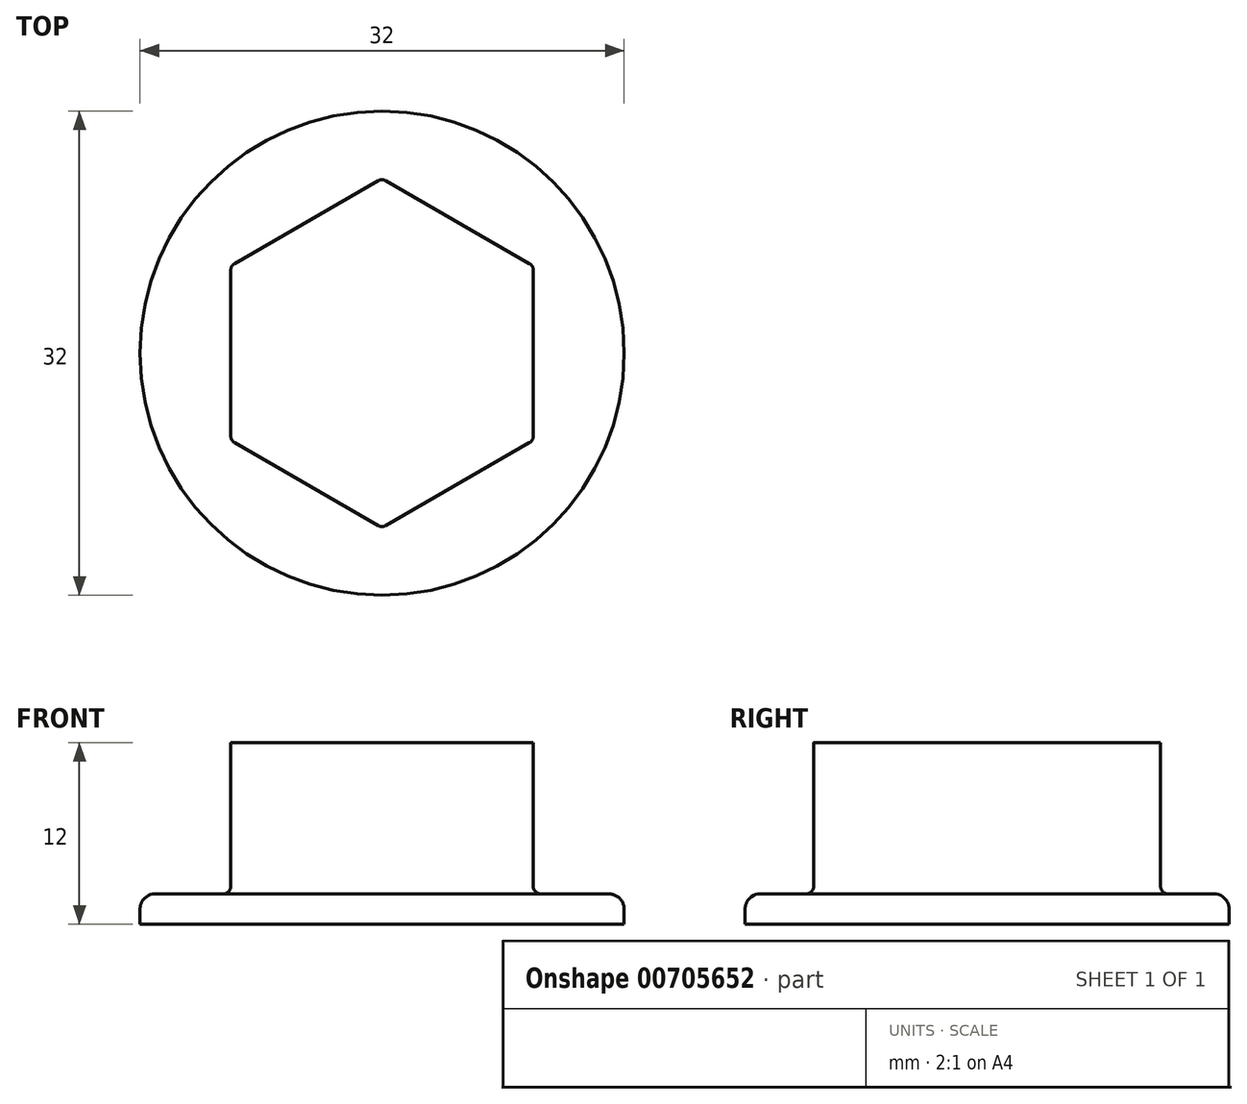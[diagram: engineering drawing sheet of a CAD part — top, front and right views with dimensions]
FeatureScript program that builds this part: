
annotation { "Feature Type Name" : "Feature", "Feature Type Description" : "" }
export const myFeature = defineFeature(function(context is Context, id is Id, definition is map)
    precondition{}
    {
        {
            var Q0;
            Q0=qCreatedBy(makeId("Top.planeOp"),FACE);
            var sketch = newSketch(context, id + "F0", { "sketchPlane" : qUnion([Q0])});
            skCircle(sketch, "E0", {"center": v(0, 0) * mm, "radius": 16 * mm});
            skCircle(sketch, "E1.cCircle", {"center": v(0, 0) * mm, "radius": 10 * mm, "construction": true});
            skLineSegment(sketch, "E1.0", {"start": v(10, -5.77) * mm, "end": v(0, -11.55) * mm});
            skLineSegment(sketch, "E1.1", {"start": v(0, -11.55) * mm, "end": v(-10, -5.77) * mm});
            skLineSegment(sketch, "E1.2", {"start": v(-10, -5.77) * mm, "end": v(-10, 5.77) * mm});
            skLineSegment(sketch, "E1.3", {"start": v(-10, 5.77) * mm, "end": v(0, 11.55) * mm});
            skLineSegment(sketch, "E1.4", {"start": v(0, 11.55) * mm, "end": v(10, 5.77) * mm});
            skLineSegment(sketch, "E1.5", {"start": v(10, 5.77) * mm, "end": v(10, -5.77) * mm});
            skPoint(sketch, "E1.0.midPoint", {"position": v(5, -8.66) * mm});
            skSolve(sketch);
        }
        {
            var Q0;
            Q0=makeQuery(id+"F0.imprint","IMPRINT",FACE,{"disambiguationData":[TD([[makeQuery(id+"F0.imprint","IMPRINT",EDGE,{"derivedFrom":sQuery(id+"F0.wireOp",EDGE,"E0")}),1.0]])]});
            var Q1;
            Q1=makeQuery(id+"F0.imprint","IMPRINT",FACE,{"disambiguationData":[TD([[makeQuery(id+"F0.imprint","IMPRINT",EDGE,{"derivedFrom":sQuery(id+"F0.wireOp",EDGE,"E1.0")}),-1.0]])]});
            extrude(context, id + "F1", {"entities" : qUnion([Q0, Q1]), "depth" : 2 * mm, "offsetDistance" : 25 * mm});
        }
        {
            var Q0;
            Q0=makeQuery(id+"F1.opExtrude","CAP_EDGE",EDGE,{"disambiguationData":[OSD([sQuery(id+"F0.wireOp",EDGE,"E0")])],"isStart":false});
            fillet(context, id + "F2", {"entities" : qUnion([Q0]), "radius" : 1 * mm, "tangentPropagation" : true, "allowEdgeOverflow" : false});
        }
        {
            var Q0;
            Q0=makeQuery(id+"F0.imprint","IMPRINT",FACE,{"disambiguationData":[TD([[makeQuery(id+"F0.imprint","IMPRINT",EDGE,{"derivedFrom":sQuery(id+"F0.wireOp",EDGE,"E1.0")}),-1.0]])]});
            extrude(context, id + "F3", {"entities" : qUnion([Q0]), "operationType" : NewBodyOperationType.ADD, "depth" : 12 * mm, "offsetDistance" : 25 * mm});
        }
        {
            var Q0;
            Q0=makeQuery(id+"F3.boolean.opBoolean","INTERSECT",EDGE,{"derivedFrom":[makeQuery(id+"F1.opExtrude","CAP_FACE",FACE,{"disambiguationData":[OSD([sQuery(id+"F0.wireOp",EDGE,"E0")])],"isStart":false}),makeQuery(id+"F3.opExtrude","SWEPT_FACE",FACE,{"disambiguationData":[OSD([sQuery(id+"F0.wireOp",EDGE,"E1.5")])]})]});
            var Q1;
            Q1=makeQuery(id+"F3.boolean.opBoolean","INTERSECT",EDGE,{"derivedFrom":[makeQuery(id+"F1.opExtrude","CAP_FACE",FACE,{"disambiguationData":[OSD([sQuery(id+"F0.wireOp",EDGE,"E0")])],"isStart":false}),makeQuery(id+"F3.opExtrude","SWEPT_FACE",FACE,{"disambiguationData":[OSD([sQuery(id+"F0.wireOp",EDGE,"E1.0")])]})]});
            var Q2;
            Q2=makeQuery(id+"F3.opExtrude","SWEPT_EDGE",EDGE,{"disambiguationData":[OSD([sQuery(id+"F0.wireOp",EDGE,"E1.0"),sQuery(id+"F0.wireOp",EDGE,"E1.5")])]});
            var Q3;
            Q3=makeQuery(id+"F3.opExtrude","SWEPT_EDGE",EDGE,{"disambiguationData":[OSD([sQuery(id+"F0.wireOp",EDGE,"E1.4"),sQuery(id+"F0.wireOp",EDGE,"E1.5")])]});
            var Q4;
            Q4=makeQuery(id+"F3.boolean.opBoolean","INTERSECT",EDGE,{"derivedFrom":[makeQuery(id+"F1.opExtrude","CAP_FACE",FACE,{"disambiguationData":[OSD([sQuery(id+"F0.wireOp",EDGE,"E0")])],"isStart":false}),makeQuery(id+"F3.opExtrude","SWEPT_FACE",FACE,{"disambiguationData":[OSD([sQuery(id+"F0.wireOp",EDGE,"E1.4")])]})]});
            var Q5;
            Q5=makeQuery(id+"F3.opExtrude","SWEPT_EDGE",EDGE,{"disambiguationData":[OSD([sQuery(id+"F0.wireOp",EDGE,"E1.3"),sQuery(id+"F0.wireOp",EDGE,"E1.4")])]});
            var Q6;
            Q6=makeQuery(id+"F3.boolean.opBoolean","INTERSECT",EDGE,{"derivedFrom":[makeQuery(id+"F1.opExtrude","CAP_FACE",FACE,{"disambiguationData":[OSD([sQuery(id+"F0.wireOp",EDGE,"E0")])],"isStart":false}),makeQuery(id+"F3.opExtrude","SWEPT_FACE",FACE,{"disambiguationData":[OSD([sQuery(id+"F0.wireOp",EDGE,"E1.3")])]})]});
            var Q7;
            Q7=makeQuery(id+"F3.opExtrude","SWEPT_EDGE",EDGE,{"disambiguationData":[OSD([sQuery(id+"F0.wireOp",EDGE,"E1.2"),sQuery(id+"F0.wireOp",EDGE,"E1.3")])]});
            var Q8;
            Q8=makeQuery(id+"F3.boolean.opBoolean","INTERSECT",EDGE,{"derivedFrom":[makeQuery(id+"F1.opExtrude","CAP_FACE",FACE,{"disambiguationData":[OSD([sQuery(id+"F0.wireOp",EDGE,"E0")])],"isStart":false}),makeQuery(id+"F3.opExtrude","SWEPT_FACE",FACE,{"disambiguationData":[OSD([sQuery(id+"F0.wireOp",EDGE,"E1.2")])]})]});
            var Q9;
            Q9=makeQuery(id+"F3.opExtrude","SWEPT_EDGE",EDGE,{"disambiguationData":[OSD([sQuery(id+"F0.wireOp",EDGE,"E1.1"),sQuery(id+"F0.wireOp",EDGE,"E1.2")])]});
            var Q10;
            Q10=makeQuery(id+"F3.boolean.opBoolean","INTERSECT",EDGE,{"derivedFrom":[makeQuery(id+"F1.opExtrude","CAP_FACE",FACE,{"disambiguationData":[OSD([sQuery(id+"F0.wireOp",EDGE,"E0")])],"isStart":false}),makeQuery(id+"F3.opExtrude","SWEPT_FACE",FACE,{"disambiguationData":[OSD([sQuery(id+"F0.wireOp",EDGE,"E1.1")])]})]});
            var Q11;
            Q11=makeQuery(id+"F3.opExtrude","SWEPT_EDGE",EDGE,{"disambiguationData":[OSD([sQuery(id+"F0.wireOp",EDGE,"E1.0"),sQuery(id+"F0.wireOp",EDGE,"E1.1")])]});
            fillet(context, id + "F4", {"entities" : qUnion([Q0, Q1, Q2, Q3, Q4, Q5, Q6, Q7, Q8, Q9, Q10, Q11]), "radius" : .5 * mm, "tangentPropagation" : true, "allowEdgeOverflow" : false});
        }
    });
